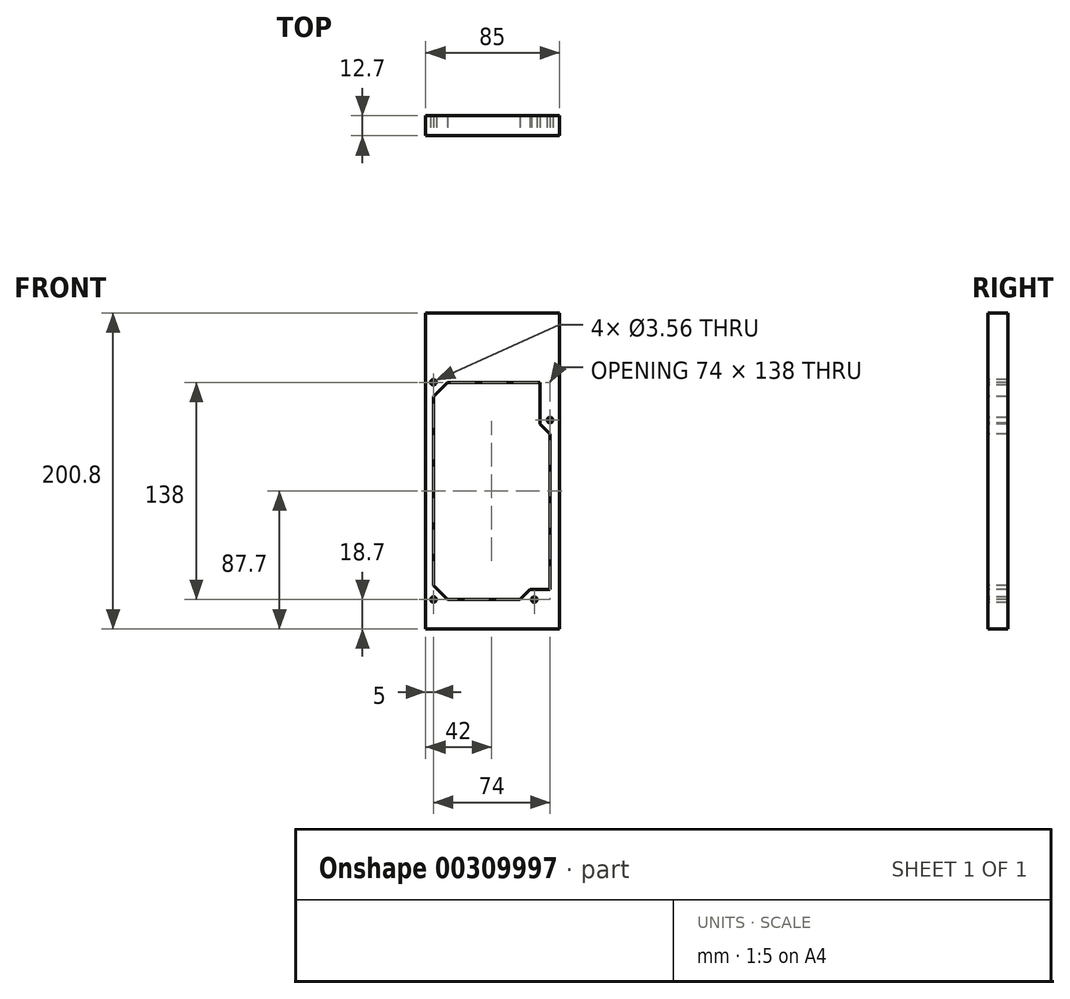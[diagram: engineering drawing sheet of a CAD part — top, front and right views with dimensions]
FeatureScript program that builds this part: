
annotation { "Feature Type Name" : "Feature", "Feature Type Description" : "" }
export const myFeature = defineFeature(function(context is Context, id is Id, definition is map)
    precondition{}
    {
        {
            var Q0;
            Q0=qCreatedBy(makeId("Front.planeOp"),FACE);
            var sketch = newSketch(context, id + "F0", { "sketchPlane" : qUnion([Q0])});
            skLineSegment(sketch, "E0.bottom", {"start": v(42.5, 100.4) * mm, "end": v(-42.5, 100.4) * mm});
            skLineSegment(sketch, "E0.top", {"start": v(42.5, -100.4) * mm, "end": v(-42.5, -100.4) * mm});
            skLineSegment(sketch, "E0.left", {"start": v(42.5, 100.4) * mm, "end": v(42.5, -100.4) * mm});
            skLineSegment(sketch, "E0.right", {"start": v(-42.5, 100.4) * mm, "end": v(-42.5, -100.4) * mm});
            skLineSegment(sketch, "E1", {"start": v(42.5, 100.4) * mm, "end": v(-42.5, -100.4) * mm, "construction": true});
            skSolve(sketch);
        }
        {
            var Q0;
            Q0=makeQuery(id+"F0.imprint","IMPRINT",FACE,{"disambiguationData":[TD([[makeQuery(id+"F0.imprint","IMPRINT",EDGE,{"derivedFrom":sQuery(id+"F0.wireOp",EDGE,"E0.bottom")}),1.0]])]});
            extrude(context, id + "F1", {"entities" : qUnion([Q0]), "depth" : 12.7 * mm});
        }
        {
            var Q0;
            Q0=makeQuery(id+"F1.opExtrude","CAP_FACE",FACE,{"disambiguationData":[OSD([sQuery(id+"F0.wireOp",EDGE,"E0.bottom"),sQuery(id+"F0.wireOp",EDGE,"E0.top"),sQuery(id+"F0.wireOp",EDGE,"E0.left"),sQuery(id+"F0.wireOp",EDGE,"E0.right")])],"isStart":false});
            var sketch = newSketch(context, id + "F2", { "sketchPlane" : qUnion([Q0])});
            skLineSegment(sketch, "E2", {"start": v(-42.5, 87.7) * mm, "end": v(42.5, 87.7) * mm, "construction": true});
            skLineSegment(sketch, "E3", {"start": v(-42.5, -87.7) * mm, "end": v(42.5, -87.7) * mm, "construction": true});
            skSolve(sketch);
        }
        {
            var Q0;
            Q0=makeQuery(id+"F2.imprint","IMPRINT",FACE,{"disambiguationData":[TD([[makeQuery(id+"F2.imprint","IMPRINT",EDGE,{"derivedFrom":makeQuery(id+"F1.opExtrude","CAP_EDGE",EDGE,{"disambiguationData":[OSD([sQuery(id+"F0.wireOp",EDGE,"E0.bottom")])],"isStart":false})}),1.0]])]});
            var sketch = newSketch(context, id + "F3", { "sketchPlane" : qUnion([Q0])});
            skPoint(sketch, "E4", {"position": v(26.5, -81.7) * mm});
            skPoint(sketch, "E5", {"position": v(-37.5, -81.7) * mm});
            skPoint(sketch, "E6", {"position": v(-37.5, 56.3) * mm});
            skPoint(sketch, "E7", {"position": v(36.5, 32.3) * mm});
            skLineSegment(sketch, "E8", {"start": v(-37.5, -81.7) * mm, "end": v(26.5, -81.7) * mm, "construction": true});
            skCircle(sketch, "E9", {"center": v(-37.5, 56.3) * mm, "radius": 1.78 * mm});
            skCircle(sketch, "E10", {"center": v(36.5, 32.3) * mm, "radius": 1.78 * mm});
            skCircle(sketch, "E11", {"center": v(26.5, -81.7) * mm, "radius": 1.78 * mm});
            skCircle(sketch, "E12", {"center": v(-37.5, -81.7) * mm, "radius": 1.78 * mm});
            skSolve(sketch);
        }
        {
            var Q0;
            Q0 = qSketchRegion(id + "F3", true);
            extrude(context, id + "F4", {"entities" : qUnion([Q0]), "operationType" : NewBodyOperationType.REMOVE, "endBound" : BoundingType.THROUGH_ALL, "oppositeDirection" : true, "depth" : 25.4 * mm});
        }
        {
            var Q0;
            Q0=makeQuery(id+"F2.imprint","IMPRINT",FACE,{"disambiguationData":[TD([[makeQuery(id+"F2.imprint","IMPRINT",EDGE,{"derivedFrom":makeQuery(id+"F1.opExtrude","CAP_EDGE",EDGE,{"disambiguationData":[OSD([sQuery(id+"F0.wireOp",EDGE,"E0.bottom")])],"isStart":false})}),1.0]])]});
            var sketch = newSketch(context, id + "F5", { "sketchPlane" : qUnion([Q0])});
            skLineSegment(sketch, "E13", {"start": v(-37.5, 47.32) * mm, "end": v(-28.52, 56.3) * mm});
            skLineSegment(sketch, "E14", {"start": v(-28.52, 56.3) * mm, "end": v(30.15, 56.3) * mm});
            skLineSegment(sketch, "E15", {"start": v(30.15, 56.3) * mm, "end": v(30.15, 29.67) * mm});
            skLineSegment(sketch, "E16", {"start": v(30.15, 29.67) * mm, "end": v(36.5, 23.32) * mm});
            skLineSegment(sketch, "E17", {"start": v(36.5, 23.32) * mm, "end": v(36.5, -75.35) * mm});
            skLineSegment(sketch, "E18", {"start": v(17.52, -81.7) * mm, "end": v(-28.52, -81.7) * mm});
            skLineSegment(sketch, "E19", {"start": v(-28.52, -81.7) * mm, "end": v(-37.5, -72.72) * mm});
            skLineSegment(sketch, "E20", {"start": v(-37.5, -72.72) * mm, "end": v(-37.5, 47.32) * mm});
            skCircle(sketch, "E21.0", {"center": v(-37.5, 56.3) * mm, "radius": 1.78 * mm, "construction": true});
            skCircle(sketch, "E22.0", {"center": v(36.5, 32.3) * mm, "radius": 1.78 * mm});
            skCircle(sketch, "E23.0", {"center": v(-37.5, -81.7) * mm, "radius": 1.78 * mm});
            skLineSegment(sketch, "E24", {"start": v(17.52, -81.7) * mm, "end": v(23.87, -75.35) * mm});
            skLineSegment(sketch, "E25", {"start": v(23.87, -75.35) * mm, "end": v(36.5, -75.35) * mm});
            skCircle(sketch, "E26.0", {"center": v(26.5, -81.7) * mm, "radius": 1.78 * mm});
            skSolve(sketch);
        }
        {
            var Q0;
            Q0 = qSketchRegion(id + "F5", true);
            extrude(context, id + "F6", {"entities" : qUnion([Q0]), "operationType" : NewBodyOperationType.REMOVE, "endBound" : BoundingType.THROUGH_ALL, "oppositeDirection" : true, "depth" : 25.4 * mm});
        }
    });
